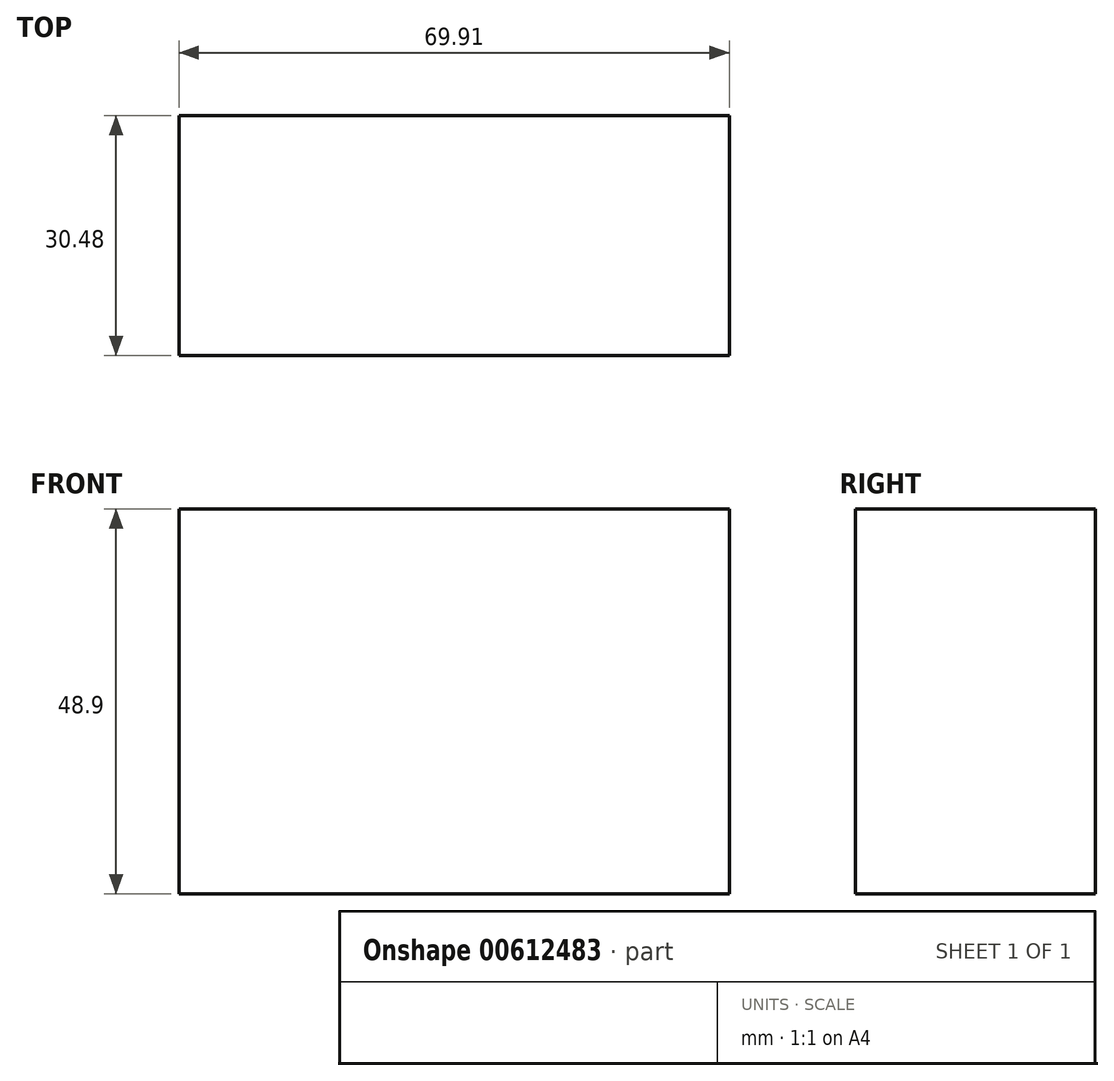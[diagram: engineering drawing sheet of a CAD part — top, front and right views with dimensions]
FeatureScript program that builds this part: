
annotation { "Feature Type Name" : "Feature", "Feature Type Description" : "" }
export const myFeature = defineFeature(function(context is Context, id is Id, definition is map)
    precondition{}
    {
        {
            var Q0;
            Q0=qCreatedBy(makeId("Front.planeOp"),FACE);
            var sketch = newSketch(context, id + "F0", { "sketchPlane" : qUnion([Q0])});
            skLineSegment(sketch, "E0.bottom", {"start": v(-85.9, 48.9) * mm, "end": v(-16, 48.9) * mm});
            skLineSegment(sketch, "E0.top", {"start": v(-85.9, 0) * mm, "end": v(-16, 0) * mm});
            skLineSegment(sketch, "E0.left", {"start": v(-85.9, 48.9) * mm, "end": v(-85.9, 0) * mm});
            skLineSegment(sketch, "E0.right", {"start": v(-16, 48.9) * mm, "end": v(-16, 0) * mm});
            skSolve(sketch);
        }
        {
            var Q0;
            Q0=makeQuery(id+"F0.imprint","IMPRINT",FACE,{"disambiguationData":[TD([[makeQuery(id+"F0.imprint","IMPRINT",EDGE,{"derivedFrom":sQuery(id+"F0.wireOp",EDGE,"E0.bottom")}),-1.0]])]});
            extrude(context, id + "F1", {"entities" : qUnion([Q0]), "depth" : 30.48 * mm, "offsetDistance" : 30.48 * mm});
        }
    });
